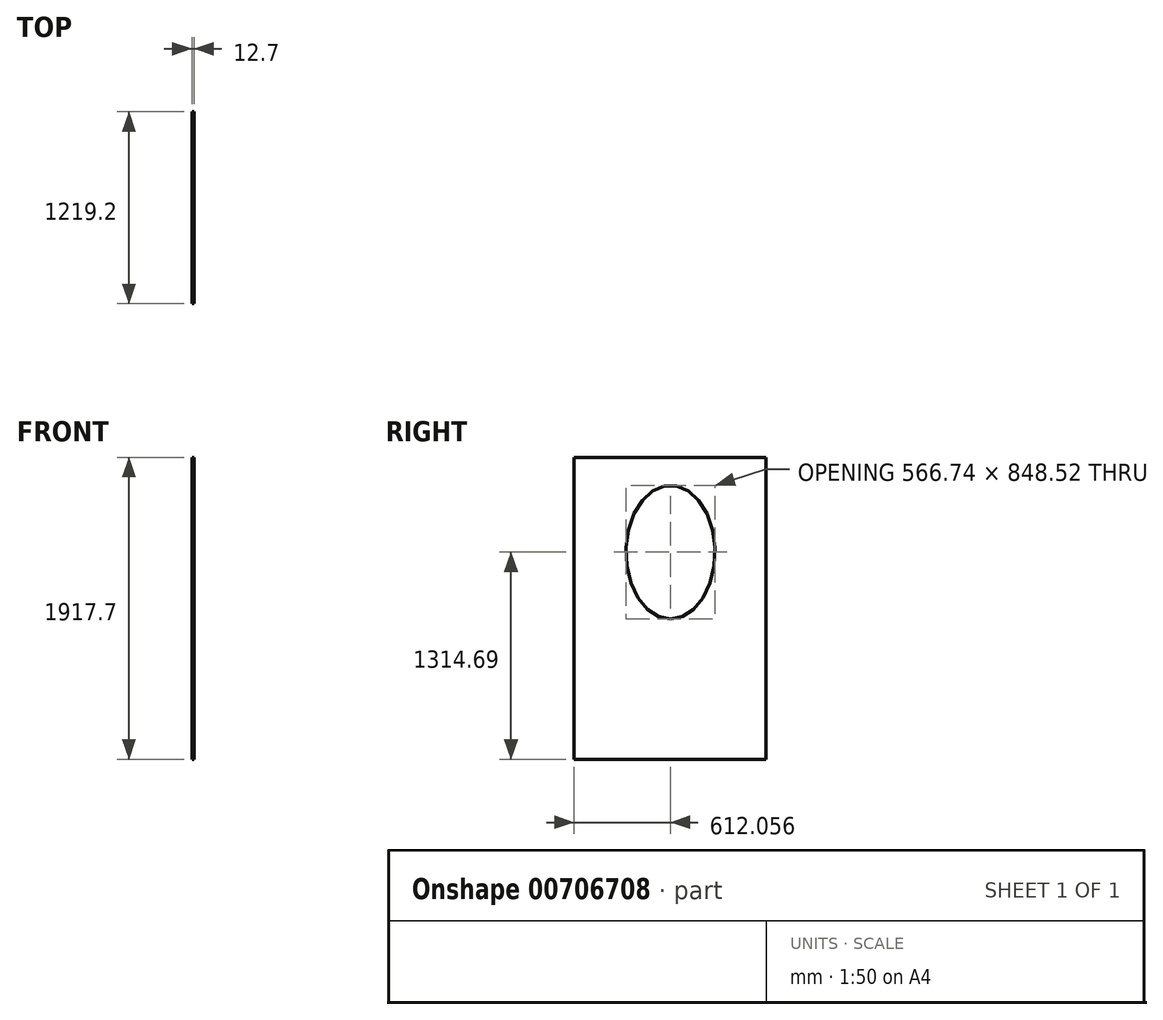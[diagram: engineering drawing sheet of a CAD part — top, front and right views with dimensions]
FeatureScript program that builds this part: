
annotation { "Feature Type Name" : "Feature", "Feature Type Description" : "" }
export const myFeature = defineFeature(function(context is Context, id is Id, definition is map)
    precondition{}
    {
        {
            var Q0;
            Q0=qCreatedBy(makeId("Right.planeOp"),FACE);
            var sketch = newSketch(context, id + "F0", { "sketchPlane" : qUnion([Q0])});
            skLineSegment(sketch, "E0.bottom", {"start": v(0, 0) * mm, "end": v(1219.2, 0) * mm});
            skLineSegment(sketch, "E0.top", {"start": v(0, 1917.7) * mm, "end": v(1219.2, 1917.7) * mm});
            skLineSegment(sketch, "E0.left", {"start": v(0, 0) * mm, "end": v(0, 1917.7) * mm});
            skLineSegment(sketch, "E0.right", {"start": v(1219.2, 0) * mm, "end": v(1219.2, 1917.7) * mm});
            skSolve(sketch);
        }
        {
            var Q0;
            Q0=makeQuery(id+"F0.imprint","IMPRINT",FACE,{"disambiguationData":[TD([[makeQuery(id+"F0.imprint","IMPRINT",EDGE,{"derivedFrom":sQuery(id+"F0.wireOp",EDGE,"E0.bottom")}),1.0]])]});
            extrude(context, id + "F1", {"entities" : qUnion([Q0]), "depth" : 12.7 * mm, "offsetDistance" : 25.4 * mm});
        }
        {
            var Q0;
            Q0=makeQuery(id+"F1.opExtrude","CAP_FACE",FACE,{"disambiguationData":[OSD([sQuery(id+"F0.wireOp",EDGE,"E0.bottom"),sQuery(id+"F0.wireOp",EDGE,"E0.top"),sQuery(id+"F0.wireOp",EDGE,"E0.left"),sQuery(id+"F0.wireOp",EDGE,"E0.right")])],"isStart":false});
            var sketch = newSketch(context, id + "F2", { "sketchPlane" : qUnion([Q0])});
            skEllipse(sketch, "E1", {"center": v(612.06, 1314.7) * mm, "majorRadius": 424.26 * mm, "minorRadius": 283.37 * mm, "majorAxis": v(0, -1)});
            skSolve(sketch);
        }
        {
            var Q0;
            Q0=makeQuery(id+"F2.imprint","IMPRINT",FACE,{"disambiguationData":[TD([[makeQuery(id+"F2.imprint","IMPRINT",EDGE,{"derivedFrom":sQuery(id+"F2.wireOp",EDGE,"E1")}),1.0]])]});
            var Q1;
            Q1=sQuery(id+"F2.wireOp",EDGE,"E1");
            extrude(context, id + "F3", {"entities" : qUnion([Q0]), "operationType" : NewBodyOperationType.REMOVE, "surfaceEntities" : qUnion([Q1]), "oppositeDirection" : true, "depth" : 12.7 * mm, "offsetDistance" : 25.4 * mm});
        }
    });
